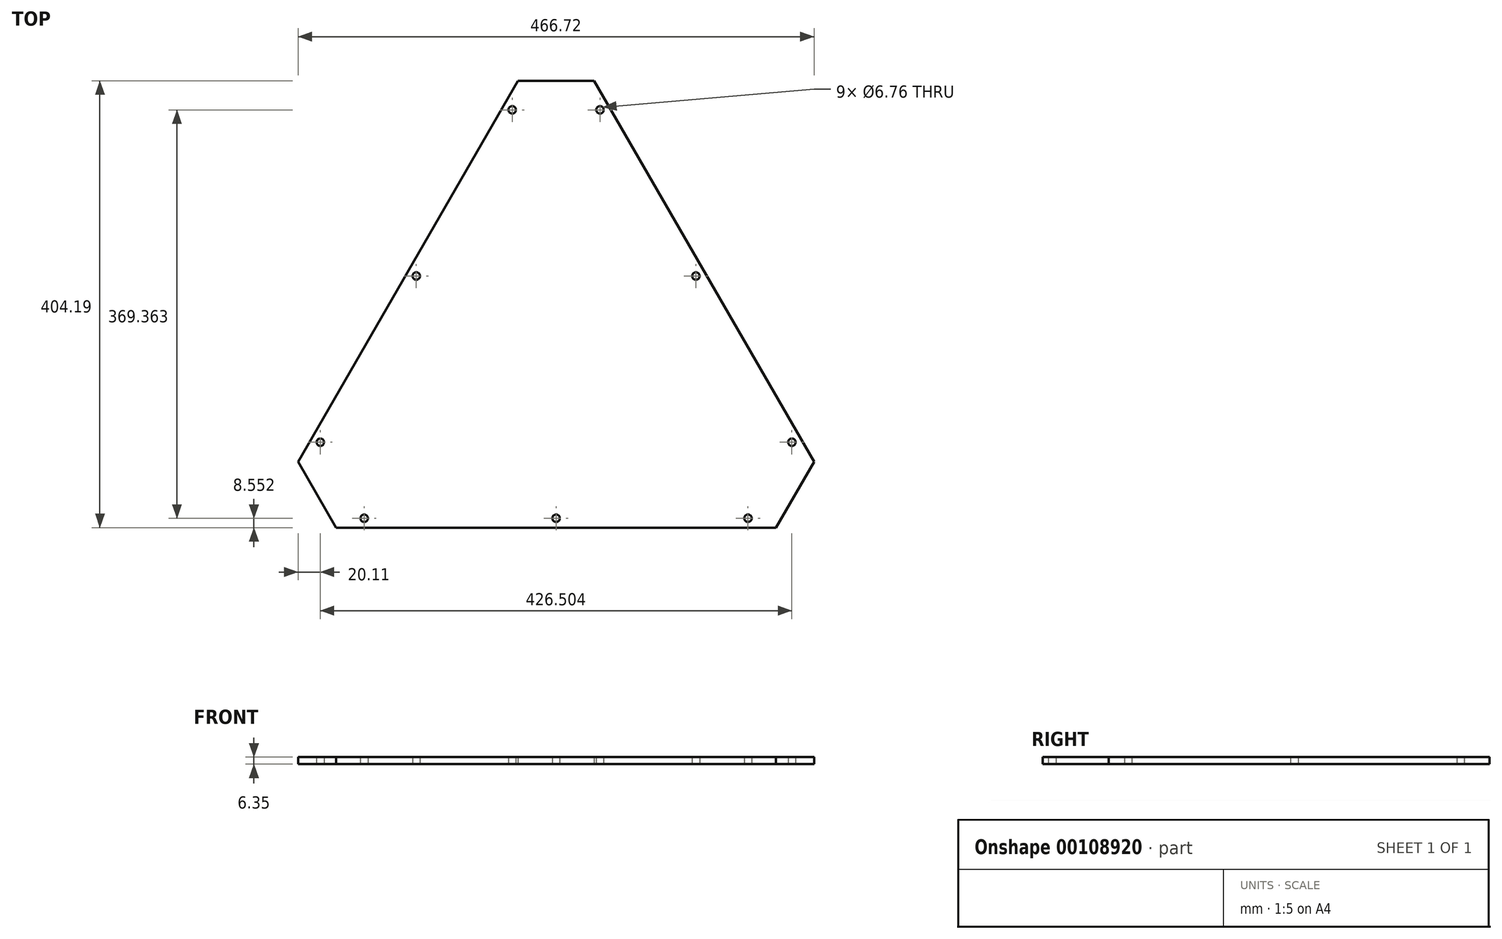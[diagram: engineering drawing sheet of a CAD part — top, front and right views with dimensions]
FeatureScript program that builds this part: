
annotation { "Feature Type Name" : "Feature", "Feature Type Description" : "" }
export const myFeature = defineFeature(function(context is Context, id is Id, definition is map)
    precondition{}
    {
        {
            var Q0;
            Q0=qCreatedBy(makeId("Top.planeOp"),FACE);
            var sketch = newSketch(context, id + "F0", { "sketchPlane" : qUnion([Q0])});
            skLineSegment(sketch, "E0", {"start": v(-800.3, 325.73) * mm, "end": v(-275.98, 284.96) * mm});
            skLineSegment(sketch, "E1", {"start": v(-247.83, 279.89) * mm, "end": v(-203.27, 294.61) * mm});
            skLineSegment(sketch, "E2", {"start": v(-176.43, 292.86) * mm, "end": v(65.3, 325.73) * mm});
            skLineSegment(sketch, "E3", {"start": v(-800.3, 325.73) * mm, "end": v(-806.6, 332.02) * mm});
            skLineSegment(sketch, "E4", {"start": v(-806.6, -332.02) * mm, "end": v(792.8, -332.02) * mm});
            skLineSegment(sketch, "E5", {"start": v(65.3, 325.73) * mm, "end": v(792.8, 332.02) * mm});
            skLineSegment(sketch, "E6", {"start": v(-443.72, -75.85) * mm, "end": v(-409.32, -135.43) * mm});
            skLineSegment(sketch, "E7", {"start": v(23, -75.85) * mm, "end": v(-11.4, -135.43) * mm});
            skLineSegment(sketch, "E8", {"start": v(-244.76, 268.76) * mm, "end": v(-175.96, 268.76) * mm});
            skLineSegment(sketch, "E9", {"start": v(-413.91, -24.22) * mm, "end": v(-395.4, -34.9) * mm});
            skArc(sketch, "E10", {"start": v(576.61, -126.88) * mm, "mid": v(573.23, -123.5) * mm, "end": v(569.85, -126.88) * mm});
            skArc(sketch, "E11", {"start": v(569.85, -126.88) * mm, "mid": v(573.23, -130.26) * mm, "end": v(576.61, -126.88) * mm});
            skArc(sketch, "E12", {"start": v(403.05, -126.88) * mm, "mid": v(399.68, -123.5) * mm, "end": v(396.3, -126.88) * mm});
            skArc(sketch, "E13", {"start": v(396.3, -126.88) * mm, "mid": v(399.68, -130.26) * mm, "end": v(403.05, -126.88) * mm});
            skArc(sketch, "E14", {"start": v(363.36, -58.12) * mm, "mid": v(359.98, -54.75) * mm, "end": v(356.6, -58.12) * mm});
            skArc(sketch, "E15", {"start": v(356.6, -58.12) * mm, "mid": v(359.98, -61.5) * mm, "end": v(363.36, -58.12) * mm});
            skArc(sketch, "E16", {"start": v(450.14, 92.18) * mm, "mid": v(446.76, 95.56) * mm, "end": v(443.38, 92.18) * mm});
            skArc(sketch, "E17", {"start": v(443.38, 92.18) * mm, "mid": v(446.76, 88.8) * mm, "end": v(450.14, 92.18) * mm});
            skArc(sketch, "E18", {"start": v(536.92, 242.48) * mm, "mid": v(533.54, 245.86) * mm, "end": v(530.16, 242.48) * mm});
            skArc(sketch, "E19", {"start": v(530.16, 242.48) * mm, "mid": v(533.54, 239.1) * mm, "end": v(536.92, 242.48) * mm});
            skArc(sketch, "E20", {"start": v(616.3, 242.48) * mm, "mid": v(612.93, 245.86) * mm, "end": v(609.55, 242.48) * mm});
            skArc(sketch, "E21", {"start": v(609.55, 242.48) * mm, "mid": v(612.93, 239.1) * mm, "end": v(616.3, 242.48) * mm});
            skArc(sketch, "E22", {"start": v(703.08, 92.18) * mm, "mid": v(699.7, 95.56) * mm, "end": v(696.33, 92.18) * mm});
            skArc(sketch, "E23", {"start": v(696.33, 92.18) * mm, "mid": v(699.7, 88.8) * mm, "end": v(703.08, 92.18) * mm});
            skArc(sketch, "E24", {"start": v(789.86, -58.12) * mm, "mid": v(786.48, -54.75) * mm, "end": v(783.1, -58.12) * mm});
            skArc(sketch, "E25", {"start": v(783.1, -58.12) * mm, "mid": v(786.48, -61.5) * mm, "end": v(789.86, -58.12) * mm});
            skArc(sketch, "E26", {"start": v(750.17, -126.88) * mm, "mid": v(746.79, -123.5) * mm, "end": v(743.41, -126.88) * mm});
            skArc(sketch, "E27", {"start": v(743.41, -126.88) * mm, "mid": v(746.79, -130.26) * mm, "end": v(750.17, -126.88) * mm});
            skLineSegment(sketch, "E28", {"start": v(339.87, -75.85) * mm, "end": v(374.28, -135.43) * mm});
            skLineSegment(sketch, "E29", {"start": v(806.6, -75.85) * mm, "end": v(772.19, -135.43) * mm});
            skLineSegment(sketch, "E30", {"start": v(538.83, 268.76) * mm, "end": v(607.63, 268.76) * mm});
            skLineSegment(sketch, "E31", {"start": v(607.63, 268.76) * mm, "end": v(806.6, -75.85) * mm});
            skLineSegment(sketch, "E32", {"start": v(772.19, -135.43) * mm, "end": v(374.28, -135.43) * mm});
            skLineSegment(sketch, "E33", {"start": v(339.87, -75.85) * mm, "end": v(538.83, 268.76) * mm});
            skLineSegment(sketch, "E34", {"start": v(-315.56, 287.15) * mm, "end": v(-524.64, 287.15) * mm});
            skLineSegment(sketch, "E35", {"start": v(-524.64, 287.15) * mm, "end": v(-733.73, 287.15) * mm});
            skLineSegment(sketch, "E36", {"start": v(-748.25, 262) * mm, "end": v(-643.7, 80.92) * mm});
            skLineSegment(sketch, "E37", {"start": v(-643.7, 80.92) * mm, "end": v(-539.17, -100.15) * mm});
            skLineSegment(sketch, "E38", {"start": v(-510.12, -100.15) * mm, "end": v(-405.58, 80.92) * mm});
            skLineSegment(sketch, "E39", {"start": v(-405.58, 80.92) * mm, "end": v(-301.04, 262) * mm});
            skArc(sketch, "E40", {"start": v(-249.4, 275.1) * mm, "mid": v(-249, 277.56) * mm, "end": v(-249.09, 280.05) * mm});
            skArc(sketch, "E41", {"start": v(-255.33, 267.4) * mm, "mid": v(-251.6, 270.66) * mm, "end": v(-249.4, 275.1) * mm});
            skLineSegment(sketch, "E42", {"start": v(-255.33, 267.4) * mm, "end": v(-286.64, 249.32) * mm});
            skArc(sketch, "E43", {"start": v(-286.64, 249.32) * mm, "mid": v(-289.27, 247.3) * mm, "end": v(-291.28, 244.67) * mm});
            skLineSegment(sketch, "E44", {"start": v(-291.28, 244.67) * mm, "end": v(-490.24, -99.93) * mm});
            skArc(sketch, "E45", {"start": v(-490.24, -99.93) * mm, "mid": v(-491.51, -103) * mm, "end": v(-491.94, -106.28) * mm});
            skLineSegment(sketch, "E46", {"start": v(-491.94, -106.28) * mm, "end": v(-491.94, -142.43) * mm});
            skArc(sketch, "E47", {"start": v(-504.64, -155.13) * mm, "mid": v(-495.66, -151.41) * mm, "end": v(-491.94, -142.43) * mm});
            skLineSegment(sketch, "E48", {"start": v(-504.64, -155.13) * mm, "end": v(-524.64, -155.13) * mm});
            skLineSegment(sketch, "E49", {"start": v(-524.64, -155.13) * mm, "end": v(-544.64, -155.13) * mm});
            skArc(sketch, "E50", {"start": v(-557.34, -142.43) * mm, "mid": v(-553.62, -151.41) * mm, "end": v(-544.64, -155.13) * mm});
            skLineSegment(sketch, "E51", {"start": v(-557.34, -142.43) * mm, "end": v(-557.34, -106.28) * mm});
            skArc(sketch, "E52", {"start": v(-557.34, -106.28) * mm, "mid": v(-557.78, -103) * mm, "end": v(-559.04, -99.93) * mm});
            skLineSegment(sketch, "E53", {"start": v(-559.04, -99.93) * mm, "end": v(-758, 244.67) * mm});
            skArc(sketch, "E54", {"start": v(-758, 244.67) * mm, "mid": v(-760.02, 247.3) * mm, "end": v(-762.65, 249.32) * mm});
            skLineSegment(sketch, "E55", {"start": v(-762.65, 249.32) * mm, "end": v(-793.96, 267.4) * mm});
            skArc(sketch, "E56", {"start": v(-798.6, 284.74) * mm, "mid": v(-799.88, 275.1) * mm, "end": v(-793.96, 267.4) * mm});
            skLineSegment(sketch, "E57", {"start": v(-798.6, 284.74) * mm, "end": v(-778.6, 319.39) * mm});
            skArc(sketch, "E58", {"start": v(-761.26, 324.03) * mm, "mid": v(-770.9, 325.3) * mm, "end": v(-778.6, 319.39) * mm});
            skLineSegment(sketch, "E59", {"start": v(-761.26, 324.03) * mm, "end": v(-729.95, 305.96) * mm});
            skArc(sketch, "E60", {"start": v(-729.95, 305.96) * mm, "mid": v(-726.89, 304.69) * mm, "end": v(-723.6, 304.26) * mm});
            skLineSegment(sketch, "E61", {"start": v(-723.6, 304.26) * mm, "end": v(-325.69, 304.26) * mm});
            skArc(sketch, "E62", {"start": v(-325.69, 304.26) * mm, "mid": v(-322.4, 304.69) * mm, "end": v(-319.34, 305.96) * mm});
            skLineSegment(sketch, "E63", {"start": v(-319.34, 305.96) * mm, "end": v(-288.03, 324.03) * mm});
            skArc(sketch, "E64", {"start": v(-270.68, 319.39) * mm, "mid": v(-278.4, 325.3) * mm, "end": v(-288.03, 324.03) * mm});
            skLineSegment(sketch, "E65", {"start": v(-270.68, 319.39) * mm, "end": v(-250.68, 284.74) * mm});
            skArc(sketch, "E66", {"start": v(-249.09, 280.05) * mm, "mid": v(-249.65, 282.48) * mm, "end": v(-250.68, 284.74) * mm});
            skLineSegment(sketch, "E67", {"start": v(-224.89, 268.97) * mm, "end": v(-433.97, -93.17) * mm});
            skLineSegment(sketch, "E68", {"start": v(-419.44, -118.33) * mm, "end": v(-210.36, -118.33) * mm});
            skLineSegment(sketch, "E69", {"start": v(-210.36, -118.33) * mm, "end": v(-1.28, -118.33) * mm});
            skLineSegment(sketch, "E70", {"start": v(13.25, -93.17) * mm, "end": v(-195.83, 268.97) * mm});
            skLineSegment(sketch, "E71", {"start": v(-177.66, 293.18) * mm, "end": v(-177.66, 275.1) * mm});
            skArc(sketch, "E72", {"start": v(-177.66, 275.1) * mm, "mid": v(-177.23, 271.82) * mm, "end": v(-175.96, 268.76) * mm});
            skLineSegment(sketch, "E73", {"start": v(-175.96, 268.76) * mm, "end": v(23, -75.85) * mm});
            skArc(sketch, "E74", {"start": v(23, -75.85) * mm, "mid": v(25.02, -78.48) * mm, "end": v(27.65, -80.5) * mm});
            skLineSegment(sketch, "E75", {"start": v(27.65, -80.5) * mm, "end": v(58.96, -98.57) * mm});
            skArc(sketch, "E76", {"start": v(63.6, -115.92) * mm, "mid": v(64.87, -106.28) * mm, "end": v(58.96, -98.57) * mm});
            skLineSegment(sketch, "E77", {"start": v(63.6, -115.92) * mm, "end": v(43.6, -150.56) * mm});
            skArc(sketch, "E78", {"start": v(26.26, -155.2) * mm, "mid": v(35.9, -156.48) * mm, "end": v(43.6, -150.56) * mm});
            skLineSegment(sketch, "E79", {"start": v(26.26, -155.2) * mm, "end": v(-5.05, -137.13) * mm});
            skArc(sketch, "E80", {"start": v(-5.05, -137.13) * mm, "mid": v(-8.12, -135.86) * mm, "end": v(-11.4, -135.43) * mm});
            skLineSegment(sketch, "E81", {"start": v(-11.4, -135.43) * mm, "end": v(-409.32, -135.43) * mm});
            skArc(sketch, "E82", {"start": v(-409.32, -135.43) * mm, "mid": v(-412.6, -135.86) * mm, "end": v(-415.67, -137.13) * mm});
            skLineSegment(sketch, "E83", {"start": v(-415.67, -137.13) * mm, "end": v(-446.98, -155.2) * mm});
            skArc(sketch, "E84", {"start": v(-464.32, -150.56) * mm, "mid": v(-456.61, -156.48) * mm, "end": v(-446.98, -155.2) * mm});
            skLineSegment(sketch, "E85", {"start": v(-464.32, -150.56) * mm, "end": v(-474.32, -133.24) * mm});
            skLineSegment(sketch, "E86", {"start": v(-474.32, -133.24) * mm, "end": v(-484.32, -115.92) * mm});
            skArc(sketch, "E87", {"start": v(-479.68, -98.57) * mm, "mid": v(-485.6, -106.28) * mm, "end": v(-484.32, -115.92) * mm});
            skLineSegment(sketch, "E88", {"start": v(-479.68, -98.57) * mm, "end": v(-448.37, -80.5) * mm});
            skArc(sketch, "E89", {"start": v(-448.37, -80.5) * mm, "mid": v(-445.74, -78.48) * mm, "end": v(-443.72, -75.85) * mm});
            skLineSegment(sketch, "E90", {"start": v(-443.72, -75.85) * mm, "end": v(-413.91, -24.22) * mm});
            skArc(sketch, "E91", {"start": v(-244.76, 268.76) * mm, "mid": v(-243.5, 271.82) * mm, "end": v(-243.06, 275.1) * mm});
            skLineSegment(sketch, "E92", {"start": v(-243.06, 275.1) * mm, "end": v(-243.06, 311.26) * mm});
            skArc(sketch, "E93", {"start": v(-230.36, 323.96) * mm, "mid": v(-239.34, 320.24) * mm, "end": v(-243.06, 311.26) * mm});
            skLineSegment(sketch, "E94", {"start": v(-230.36, 323.96) * mm, "end": v(-190.36, 323.96) * mm});
            skArc(sketch, "E95", {"start": v(-177.66, 311.26) * mm, "mid": v(-181.38, 320.24) * mm, "end": v(-190.36, 323.96) * mm});
            skLineSegment(sketch, "E96", {"start": v(-177.66, 311.26) * mm, "end": v(-177.66, 293.18) * mm});
            skLineSegment(sketch, "E97", {"start": v(-413.91, -24.22) * mm, "end": v(-244.76, 268.76) * mm});
            skArc(sketch, "E98", {"start": v(-540.49, -102.43) * mm, "mid": v(-539.17, -101.67) * mm, "end": v(-539.17, -100.15) * mm});
            skArc(sketch, "E99", {"start": v(-510.12, -100.15) * mm, "mid": v(-510.12, -101.67) * mm, "end": v(-508.8, -102.43) * mm});
            skLineSegment(sketch, "E100", {"start": v(-277.88, 288.26) * mm, "end": v(-281.23, 294.07) * mm});
            skLineSegment(sketch, "E101", {"start": v(-281.23, 294.07) * mm, "end": v(-273.35, 298.62) * mm});
            skLineSegment(sketch, "E102", {"start": v(-273.35, 298.62) * mm, "end": v(-281.45, 312.65) * mm});
            skArc(sketch, "E103", {"start": v(-281.45, 312.65) * mm, "mid": v(-281.3, 313.26) * mm, "end": v(-281.9, 313.42) * mm});
            skArc(sketch, "E104", {"start": v(-281.9, 313.42) * mm, "mid": v(-282.1, 313.15) * mm, "end": v(-282.06, 312.81) * mm});
            skLineSegment(sketch, "E105", {"start": v(-282.06, 312.81) * mm, "end": v(-296.1, 304.71) * mm});
            skLineSegment(sketch, "E106", {"start": v(-296.1, 304.71) * mm, "end": v(-291.55, 296.83) * mm});
            skLineSegment(sketch, "E107", {"start": v(-291.55, 296.83) * mm, "end": v(-297.35, 293.48) * mm});
            skLineSegment(sketch, "E108", {"start": v(-297.35, 293.48) * mm, "end": v(-301.9, 301.36) * mm});
            skLineSegment(sketch, "E109", {"start": v(-301.9, 301.36) * mm, "end": v(-315.93, 293.26) * mm});
            skArc(sketch, "E110", {"start": v(-315.93, 293.26) * mm, "mid": v(-316.2, 293.47) * mm, "end": v(-316.54, 293.42) * mm});
            skArc(sketch, "E111", {"start": v(-316.54, 293.42) * mm, "mid": v(-316.7, 292.81) * mm, "end": v(-316.1, 292.65) * mm});
            skLineSegment(sketch, "E112", {"start": v(-316.1, 292.65) * mm, "end": v(-314.24, 289.44) * mm});
            skArc(sketch, "E113", {"start": v(-315.56, 287.15) * mm, "mid": v(-314.24, 287.91) * mm, "end": v(-314.24, 289.44) * mm});
            skArc(sketch, "E114", {"start": v(-735.05, 289.44) * mm, "mid": v(-735.05, 287.91) * mm, "end": v(-733.73, 287.15) * mm});
            skLineSegment(sketch, "E115", {"start": v(-735.05, 289.44) * mm, "end": v(-733.2, 292.65) * mm});
            skArc(sketch, "E116", {"start": v(-733.2, 292.65) * mm, "mid": v(-732.58, 292.81) * mm, "end": v(-732.75, 293.42) * mm});
            skArc(sketch, "E117", {"start": v(-732.75, 293.42) * mm, "mid": v(-733.08, 293.47) * mm, "end": v(-733.35, 293.26) * mm});
            skLineSegment(sketch, "E118", {"start": v(-733.35, 293.26) * mm, "end": v(-747.39, 301.36) * mm});
            skLineSegment(sketch, "E119", {"start": v(-747.39, 301.36) * mm, "end": v(-751.94, 293.48) * mm});
            skLineSegment(sketch, "E120", {"start": v(-751.94, 293.48) * mm, "end": v(-754.84, 295.16) * mm});
            skLineSegment(sketch, "E121", {"start": v(-754.84, 295.16) * mm, "end": v(-757.74, 296.83) * mm});
            skLineSegment(sketch, "E122", {"start": v(-757.74, 296.83) * mm, "end": v(-753.19, 304.71) * mm});
            skLineSegment(sketch, "E123", {"start": v(-753.19, 304.71) * mm, "end": v(-767.22, 312.81) * mm});
            skArc(sketch, "E124", {"start": v(-767.22, 312.81) * mm, "mid": v(-767.18, 313.15) * mm, "end": v(-767.39, 313.42) * mm});
            skArc(sketch, "E125", {"start": v(-767.39, 313.42) * mm, "mid": v(-768, 313.26) * mm, "end": v(-767.83, 312.65) * mm});
            skLineSegment(sketch, "E126", {"start": v(-767.83, 312.65) * mm, "end": v(-775.93, 298.62) * mm});
            skLineSegment(sketch, "E127", {"start": v(-775.93, 298.62) * mm, "end": v(-768.05, 294.07) * mm});
            skLineSegment(sketch, "E128", {"start": v(-768.05, 294.07) * mm, "end": v(-771.4, 288.26) * mm});
            skLineSegment(sketch, "E129", {"start": v(-771.4, 288.26) * mm, "end": v(-779.28, 292.81) * mm});
            skLineSegment(sketch, "E130", {"start": v(-779.28, 292.81) * mm, "end": v(-787.39, 278.78) * mm});
            skArc(sketch, "E131", {"start": v(-787.39, 278.78) * mm, "mid": v(-788, 278.62) * mm, "end": v(-787.83, 278) * mm});
            skArc(sketch, "E132", {"start": v(-787.83, 278) * mm, "mid": v(-787.5, 277.97) * mm, "end": v(-787.22, 278.17) * mm});
            skLineSegment(sketch, "E133", {"start": v(-787.22, 278.17) * mm, "end": v(-773.19, 270.07) * mm});
            skLineSegment(sketch, "E134", {"start": v(-773.19, 270.07) * mm, "end": v(-768.64, 277.95) * mm});
            skLineSegment(sketch, "E135", {"start": v(-768.64, 277.95) * mm, "end": v(-765.74, 276.28) * mm});
            skLineSegment(sketch, "E136", {"start": v(-765.74, 276.28) * mm, "end": v(-762.84, 274.6) * mm});
            skLineSegment(sketch, "E137", {"start": v(-762.84, 274.6) * mm, "end": v(-767.39, 266.72) * mm});
            skLineSegment(sketch, "E138", {"start": v(-767.39, 266.72) * mm, "end": v(-753.35, 258.62) * mm});
            skArc(sketch, "E139", {"start": v(-753.35, 258.62) * mm, "mid": v(-753.4, 258.28) * mm, "end": v(-753.2, 258) * mm});
            skArc(sketch, "E140", {"start": v(-753.2, 258) * mm, "mid": v(-752.58, 258.17) * mm, "end": v(-752.75, 258.78) * mm});
            skLineSegment(sketch, "E141", {"start": v(-752.75, 258.78) * mm, "end": v(-750.9, 262) * mm});
            skArc(sketch, "E142", {"start": v(-748.25, 262) * mm, "mid": v(-749.57, 262.76) * mm, "end": v(-750.9, 262) * mm});
            skLineSegment(sketch, "E143", {"start": v(-540.49, -102.43) * mm, "end": v(-544.2, -102.43) * mm});
            skArc(sketch, "E144", {"start": v(-544.2, -102.43) * mm, "mid": v(-544.64, -102) * mm, "end": v(-545.09, -102.43) * mm});
            skArc(sketch, "E145", {"start": v(-545.09, -102.43) * mm, "mid": v(-544.96, -102.75) * mm, "end": v(-544.64, -102.88) * mm});
            skLineSegment(sketch, "E146", {"start": v(-544.64, -102.88) * mm, "end": v(-544.64, -119.08) * mm});
            skLineSegment(sketch, "E147", {"start": v(-544.64, -119.08) * mm, "end": v(-535.54, -119.08) * mm});
            skLineSegment(sketch, "E148", {"start": v(-535.54, -119.08) * mm, "end": v(-535.54, -125.78) * mm});
            skLineSegment(sketch, "E149", {"start": v(-535.54, -125.78) * mm, "end": v(-544.64, -125.78) * mm});
            skLineSegment(sketch, "E150", {"start": v(-544.64, -125.78) * mm, "end": v(-544.64, -142) * mm});
            skArc(sketch, "E151", {"start": v(-544.64, -142) * mm, "mid": v(-544.96, -142.12) * mm, "end": v(-545.09, -142.43) * mm});
            skArc(sketch, "E152", {"start": v(-545.09, -142.43) * mm, "mid": v(-544.64, -142.88) * mm, "end": v(-544.2, -142.43) * mm});
            skLineSegment(sketch, "E153", {"start": v(-544.2, -142.43) * mm, "end": v(-528, -142.43) * mm});
            skLineSegment(sketch, "E154", {"start": v(-528, -142.43) * mm, "end": v(-528, -133.33) * mm});
            skLineSegment(sketch, "E155", {"start": v(-528, -133.33) * mm, "end": v(-521.3, -133.33) * mm});
            skLineSegment(sketch, "E156", {"start": v(-521.3, -133.33) * mm, "end": v(-521.3, -142.43) * mm});
            skLineSegment(sketch, "E157", {"start": v(-521.3, -142.43) * mm, "end": v(-505.09, -142.43) * mm});
            skArc(sketch, "E158", {"start": v(-505.09, -142.43) * mm, "mid": v(-504.64, -142.88) * mm, "end": v(-504.2, -142.43) * mm});
            skArc(sketch, "E159", {"start": v(-504.2, -142.43) * mm, "mid": v(-504.33, -142.12) * mm, "end": v(-504.64, -142) * mm});
            skLineSegment(sketch, "E160", {"start": v(-504.64, -142) * mm, "end": v(-504.64, -125.78) * mm});
            skLineSegment(sketch, "E161", {"start": v(-504.64, -125.78) * mm, "end": v(-513.74, -125.78) * mm});
            skLineSegment(sketch, "E162", {"start": v(-513.74, -125.78) * mm, "end": v(-513.74, -119.08) * mm});
            skLineSegment(sketch, "E163", {"start": v(-513.74, -119.08) * mm, "end": v(-504.64, -119.08) * mm});
            skLineSegment(sketch, "E164", {"start": v(-504.64, -119.08) * mm, "end": v(-504.64, -102.88) * mm});
            skArc(sketch, "E165", {"start": v(-504.64, -102.88) * mm, "mid": v(-504.33, -102.75) * mm, "end": v(-504.2, -102.43) * mm});
            skArc(sketch, "E166", {"start": v(-504.2, -102.43) * mm, "mid": v(-504.64, -102) * mm, "end": v(-505.09, -102.43) * mm});
            skLineSegment(sketch, "E167", {"start": v(-505.09, -102.43) * mm, "end": v(-508.8, -102.43) * mm});
            skArc(sketch, "E168", {"start": v(-298.4, 262) * mm, "mid": v(-299.72, 262.76) * mm, "end": v(-301.04, 262) * mm});
            skLineSegment(sketch, "E169", {"start": v(-298.4, 262) * mm, "end": v(-296.54, 258.78) * mm});
            skArc(sketch, "E170", {"start": v(-296.54, 258.78) * mm, "mid": v(-296.7, 258.17) * mm, "end": v(-296.1, 258) * mm});
            skArc(sketch, "E171", {"start": v(-296.1, 258) * mm, "mid": v(-295.89, 258.28) * mm, "end": v(-295.93, 258.62) * mm});
            skLineSegment(sketch, "E172", {"start": v(-295.93, 258.62) * mm, "end": v(-281.9, 266.72) * mm});
            skLineSegment(sketch, "E173", {"start": v(-281.9, 266.72) * mm, "end": v(-286.45, 274.6) * mm});
            skLineSegment(sketch, "E174", {"start": v(-286.45, 274.6) * mm, "end": v(-280.65, 277.95) * mm});
            skLineSegment(sketch, "E175", {"start": v(-280.65, 277.95) * mm, "end": v(-276.1, 270.07) * mm});
            skLineSegment(sketch, "E176", {"start": v(-276.1, 270.07) * mm, "end": v(-262.06, 278.17) * mm});
            skArc(sketch, "E177", {"start": v(-262.06, 278.17) * mm, "mid": v(-261.8, 277.97) * mm, "end": v(-261.45, 278) * mm});
            skArc(sketch, "E178", {"start": v(-261.45, 278) * mm, "mid": v(-261.3, 278.62) * mm, "end": v(-261.9, 278.78) * mm});
            skLineSegment(sketch, "E179", {"start": v(-261.9, 278.78) * mm, "end": v(-270, 292.81) * mm});
            skLineSegment(sketch, "E180", {"start": v(-270, 292.81) * mm, "end": v(-277.88, 288.26) * mm});
            skLineSegment(sketch, "E181", {"start": v(-199.46, 294.61) * mm, "end": v(-190.36, 294.61) * mm});
            skLineSegment(sketch, "E182", {"start": v(-190.36, 294.61) * mm, "end": v(-190.36, 310.82) * mm});
            skArc(sketch, "E183", {"start": v(-190.36, 310.82) * mm, "mid": v(-190.05, 310.95) * mm, "end": v(-189.92, 311.26) * mm});
            skArc(sketch, "E184", {"start": v(-189.92, 311.26) * mm, "mid": v(-190.36, 311.7) * mm, "end": v(-190.8, 311.26) * mm});
            skLineSegment(sketch, "E185", {"start": v(-190.8, 311.26) * mm, "end": v(-207, 311.26) * mm});
            skLineSegment(sketch, "E186", {"start": v(-207, 311.26) * mm, "end": v(-207, 302.16) * mm});
            skLineSegment(sketch, "E187", {"start": v(-207, 302.16) * mm, "end": v(-213.7, 302.16) * mm});
            skLineSegment(sketch, "E188", {"start": v(-213.7, 302.16) * mm, "end": v(-213.7, 311.26) * mm});
            skLineSegment(sketch, "E189", {"start": v(-213.7, 311.26) * mm, "end": v(-226.2, 311.26) * mm});
            skLineSegment(sketch, "E190", {"start": v(-226.2, 311.26) * mm, "end": v(-229.92, 311.26) * mm});
            skArc(sketch, "E191", {"start": v(-229.92, 311.26) * mm, "mid": v(-230.36, 311.7) * mm, "end": v(-230.8, 311.26) * mm});
            skArc(sketch, "E192", {"start": v(-230.8, 311.26) * mm, "mid": v(-230.67, 310.95) * mm, "end": v(-230.36, 310.82) * mm});
            skLineSegment(sketch, "E193", {"start": v(-230.36, 310.82) * mm, "end": v(-230.36, 294.61) * mm});
            skLineSegment(sketch, "E194", {"start": v(-230.36, 294.61) * mm, "end": v(-221.26, 294.61) * mm});
            skLineSegment(sketch, "E195", {"start": v(-221.26, 294.61) * mm, "end": v(-221.26, 287.91) * mm});
            skLineSegment(sketch, "E196", {"start": v(-221.26, 287.91) * mm, "end": v(-226.2, 287.91) * mm});
            skLineSegment(sketch, "E197", {"start": v(-226.2, 287.91) * mm, "end": v(-230.36, 287.91) * mm});
            skLineSegment(sketch, "E198", {"start": v(-230.36, 287.91) * mm, "end": v(-230.36, 271.7) * mm});
            skArc(sketch, "E199", {"start": v(-230.36, 271.7) * mm, "mid": v(-230.67, 271.57) * mm, "end": v(-230.8, 271.26) * mm});
            skArc(sketch, "E200", {"start": v(-230.8, 271.26) * mm, "mid": v(-230.36, 270.82) * mm, "end": v(-229.92, 271.26) * mm});
            skLineSegment(sketch, "E201", {"start": v(-229.92, 271.26) * mm, "end": v(-226.2, 271.26) * mm});
            skArc(sketch, "E202", {"start": v(-224.89, 268.97) * mm, "mid": v(-224.89, 270.5) * mm, "end": v(-226.2, 271.26) * mm});
            skArc(sketch, "E203", {"start": v(-436.6, -93.17) * mm, "mid": v(-435.29, -93.93) * mm, "end": v(-433.97, -93.17) * mm});
            skLineSegment(sketch, "E204", {"start": v(-436.6, -93.17) * mm, "end": v(-438.46, -89.95) * mm});
            skArc(sketch, "E205", {"start": v(-438.46, -89.95) * mm, "mid": v(-438.3, -89.35) * mm, "end": v(-438.9, -89.18) * mm});
            skArc(sketch, "E206", {"start": v(-438.9, -89.18) * mm, "mid": v(-439.11, -89.45) * mm, "end": v(-439.07, -89.8) * mm});
            skLineSegment(sketch, "E207", {"start": v(-439.07, -89.8) * mm, "end": v(-453.1, -97.9) * mm});
            skLineSegment(sketch, "E208", {"start": v(-453.1, -97.9) * mm, "end": v(-448.55, -105.77) * mm});
            skLineSegment(sketch, "E209", {"start": v(-448.55, -105.77) * mm, "end": v(-454.36, -109.12) * mm});
            skLineSegment(sketch, "E210", {"start": v(-454.36, -109.12) * mm, "end": v(-458.9, -101.24) * mm});
            skLineSegment(sketch, "E211", {"start": v(-458.9, -101.24) * mm, "end": v(-472.94, -109.35) * mm});
            skArc(sketch, "E212", {"start": v(-472.94, -109.35) * mm, "mid": v(-473.21, -109.14) * mm, "end": v(-473.55, -109.18) * mm});
            skArc(sketch, "E213", {"start": v(-473.55, -109.18) * mm, "mid": v(-473.71, -109.8) * mm, "end": v(-473.1, -109.95) * mm});
            skLineSegment(sketch, "E214", {"start": v(-473.1, -109.95) * mm, "end": v(-465, -123.99) * mm});
            skLineSegment(sketch, "E215", {"start": v(-465, -123.99) * mm, "end": v(-457.12, -119.44) * mm});
            skLineSegment(sketch, "E216", {"start": v(-457.12, -119.44) * mm, "end": v(-453.77, -125.24) * mm});
            skLineSegment(sketch, "E217", {"start": v(-453.77, -125.24) * mm, "end": v(-461.65, -129.8) * mm});
            skLineSegment(sketch, "E218", {"start": v(-461.65, -129.8) * mm, "end": v(-453.55, -143.83) * mm});
            skArc(sketch, "E219", {"start": v(-453.55, -143.83) * mm, "mid": v(-453.71, -144.43) * mm, "end": v(-453.1, -144.6) * mm});
            skArc(sketch, "E220", {"start": v(-453.1, -144.6) * mm, "mid": v(-452.9, -144.33) * mm, "end": v(-452.94, -143.99) * mm});
            skLineSegment(sketch, "E221", {"start": v(-452.94, -143.99) * mm, "end": v(-438.9, -135.89) * mm});
            skLineSegment(sketch, "E222", {"start": v(-438.9, -135.89) * mm, "end": v(-443.46, -128) * mm});
            skLineSegment(sketch, "E223", {"start": v(-443.46, -128) * mm, "end": v(-437.65, -124.65) * mm});
            skLineSegment(sketch, "E224", {"start": v(-437.65, -124.65) * mm, "end": v(-433.1, -132.54) * mm});
            skLineSegment(sketch, "E225", {"start": v(-433.1, -132.54) * mm, "end": v(-419.07, -124.43) * mm});
            skArc(sketch, "E226", {"start": v(-419.07, -124.43) * mm, "mid": v(-418.8, -124.64) * mm, "end": v(-418.46, -124.6) * mm});
            skArc(sketch, "E227", {"start": v(-418.46, -124.6) * mm, "mid": v(-418.3, -123.99) * mm, "end": v(-418.9, -123.83) * mm});
            skLineSegment(sketch, "E228", {"start": v(-418.9, -123.83) * mm, "end": v(-420.76, -120.61) * mm});
            skArc(sketch, "E229", {"start": v(-419.44, -118.33) * mm, "mid": v(-420.76, -119.09) * mm, "end": v(-420.76, -120.61) * mm});
            skArc(sketch, "E230", {"start": v(0.04, -120.61) * mm, "mid": v(0.04, -119.09) * mm, "end": v(-1.28, -118.33) * mm});
            skLineSegment(sketch, "E231", {"start": v(0.04, -120.61) * mm, "end": v(-1.81, -123.83) * mm});
            skArc(sketch, "E232", {"start": v(-1.81, -123.83) * mm, "mid": v(-2.42, -123.99) * mm, "end": v(-2.26, -124.6) * mm});
            skArc(sketch, "E233", {"start": v(-2.26, -124.6) * mm, "mid": v(-1.92, -124.64) * mm, "end": v(-1.65, -124.43) * mm});
            skLineSegment(sketch, "E234", {"start": v(-1.65, -124.43) * mm, "end": v(12.38, -132.54) * mm});
            skLineSegment(sketch, "E235", {"start": v(12.38, -132.54) * mm, "end": v(16.93, -124.65) * mm});
            skLineSegment(sketch, "E236", {"start": v(16.93, -124.65) * mm, "end": v(22.74, -128) * mm});
            skLineSegment(sketch, "E237", {"start": v(22.74, -128) * mm, "end": v(18.19, -135.89) * mm});
            skLineSegment(sketch, "E238", {"start": v(18.19, -135.89) * mm, "end": v(32.22, -143.99) * mm});
            skArc(sketch, "E239", {"start": v(32.22, -143.99) * mm, "mid": v(32.18, -144.33) * mm, "end": v(32.38, -144.6) * mm});
            skArc(sketch, "E240", {"start": v(32.38, -144.6) * mm, "mid": v(33, -144.43) * mm, "end": v(32.83, -143.83) * mm});
            skLineSegment(sketch, "E241", {"start": v(32.83, -143.83) * mm, "end": v(40.93, -129.8) * mm});
            skLineSegment(sketch, "E242", {"start": v(40.93, -129.8) * mm, "end": v(33.05, -125.24) * mm});
            skLineSegment(sketch, "E243", {"start": v(33.05, -125.24) * mm, "end": v(36.4, -119.44) * mm});
            skLineSegment(sketch, "E244", {"start": v(36.4, -119.44) * mm, "end": v(44.28, -123.99) * mm});
            skLineSegment(sketch, "E245", {"start": v(44.28, -123.99) * mm, "end": v(52.38, -109.95) * mm});
            skArc(sketch, "E246", {"start": v(52.38, -109.95) * mm, "mid": v(53, -109.8) * mm, "end": v(52.83, -109.18) * mm});
            skArc(sketch, "E247", {"start": v(52.83, -109.18) * mm, "mid": v(52.5, -109.14) * mm, "end": v(52.22, -109.35) * mm});
            skLineSegment(sketch, "E248", {"start": v(52.22, -109.35) * mm, "end": v(38.19, -101.24) * mm});
            skLineSegment(sketch, "E249", {"start": v(38.19, -101.24) * mm, "end": v(33.64, -109.12) * mm});
            skLineSegment(sketch, "E250", {"start": v(33.64, -109.12) * mm, "end": v(27.83, -105.77) * mm});
            skLineSegment(sketch, "E251", {"start": v(27.83, -105.77) * mm, "end": v(32.38, -97.9) * mm});
            skLineSegment(sketch, "E252", {"start": v(32.38, -97.9) * mm, "end": v(18.35, -89.8) * mm});
            skArc(sketch, "E253", {"start": v(18.35, -89.8) * mm, "mid": v(18.4, -89.45) * mm, "end": v(18.19, -89.18) * mm});
            skArc(sketch, "E254", {"start": v(18.19, -89.18) * mm, "mid": v(17.58, -89.35) * mm, "end": v(17.74, -89.95) * mm});
            skLineSegment(sketch, "E255", {"start": v(17.74, -89.95) * mm, "end": v(15.89, -93.17) * mm});
            skArc(sketch, "E256", {"start": v(13.25, -93.17) * mm, "mid": v(14.57, -93.93) * mm, "end": v(15.89, -93.17) * mm});
            skArc(sketch, "E257", {"start": v(-194.51, 271.26) * mm, "mid": v(-195.83, 270.5) * mm, "end": v(-195.83, 268.97) * mm});
            skLineSegment(sketch, "E258", {"start": v(-194.51, 271.26) * mm, "end": v(-190.8, 271.26) * mm});
            skArc(sketch, "E259", {"start": v(-190.8, 271.26) * mm, "mid": v(-190.36, 270.82) * mm, "end": v(-189.92, 271.26) * mm});
            skArc(sketch, "E260", {"start": v(-189.92, 271.26) * mm, "mid": v(-190.05, 271.57) * mm, "end": v(-190.36, 271.7) * mm});
            skLineSegment(sketch, "E261", {"start": v(-190.36, 271.7) * mm, "end": v(-190.36, 287.91) * mm});
            skLineSegment(sketch, "E262", {"start": v(-190.36, 287.91) * mm, "end": v(-199.46, 287.91) * mm});
            skLineSegment(sketch, "E263", {"start": v(-199.46, 287.91) * mm, "end": v(-199.46, 294.61) * mm});
            skLineSegment(sketch, "E264", {"start": v(-275.98, 284.96) * mm, "end": v(-277.88, 288.26) * mm});
            skLineSegment(sketch, "E265", {"start": v(-277.88, 288.26) * mm, "end": v(-278.98, 287.63) * mm});
            skLineSegment(sketch, "E266", {"start": v(-245.57, 281.51) * mm, "end": v(-249.09, 280.05) * mm});
            skLineSegment(sketch, "E267", {"start": v(-249.09, 280.05) * mm, "end": v(-247.83, 279.89) * mm});
            skLineSegment(sketch, "E268", {"start": v(-203.27, 294.61) * mm, "end": v(-199.46, 294.61) * mm});
            skLineSegment(sketch, "E269", {"start": v(-199.46, 294.61) * mm, "end": v(-199.46, 295.88) * mm});
            skLineSegment(sketch, "E270", {"start": v(-173.98, 294.17) * mm, "end": v(-177.66, 293.18) * mm});
            skLineSegment(sketch, "E271", {"start": v(-177.66, 293.18) * mm, "end": v(-176.43, 292.86) * mm});
            skLineSegment(sketch, "E272", {"start": v(-278.98, 287.63) * mm, "end": v(-245.57, 281.51) * mm});
            skLineSegment(sketch, "E273", {"start": v(-199.46, 295.88) * mm, "end": v(-173.98, 294.17) * mm});
            skLineSegment(sketch, "E274", {"start": v(573.23, -135.43) * mm, "end": v(573.23, 268.76) * mm, "construction": true});
            skLineSegment(sketch, "E275", {"start": v(357.07, -105.64) * mm, "end": v(707.11, 96.46) * mm, "construction": true});
            skPoint(sketch, "E276.endSnap0", {"position": v(446.76, 95.56) * mm});
            skLineSegment(sketch, "E277", {"start": v(439.35, 96.46) * mm, "end": v(789.39, -105.64) * mm, "construction": true});
            skSolve(sketch);
        }
        {
            var Q0;
            Q0=makeQuery(id+"F0.imprint","IMPRINT",FACE,{"disambiguationData":[TD([[makeQuery(id+"F0.imprint","IMPRINT",EDGE,{"derivedFrom":sQuery(id+"F0.wireOp",EDGE,"E10")}),-1.0]])]});
            extrude(context, id + "F1", {"entities" : qUnion([Q0]), "depth" : 6.35 * mm});
        }
    });
